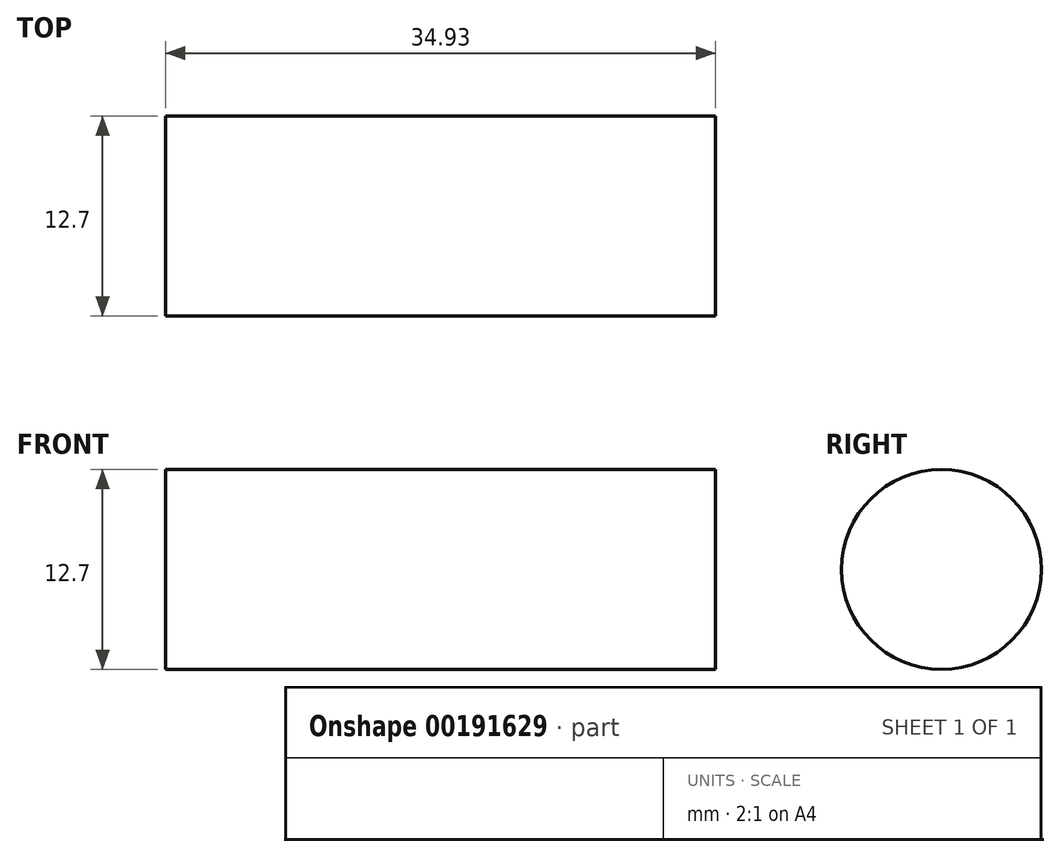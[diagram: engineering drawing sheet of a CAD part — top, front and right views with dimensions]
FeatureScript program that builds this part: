
annotation { "Feature Type Name" : "Feature", "Feature Type Description" : "" }
export const myFeature = defineFeature(function(context is Context, id is Id, definition is map)
    precondition{}
    {
        {
            var Q0;
            Q0=qCreatedBy(makeId("Right.planeOp"),FACE);
            var sketch = newSketch(context, id + "F0", { "sketchPlane" : qUnion([Q0])});
            skCircle(sketch, "E0", {"center": v(0, 0) * mm, "radius": 6.35 * mm});
            skSolve(sketch);
        }
        {
            var Q0;
            Q0=makeQuery(id+"F0.imprint","IMPRINT",FACE,{"disambiguationData":[TD([[makeQuery(id+"F0.imprint","IMPRINT",EDGE,{"derivedFrom":sQuery(id+"F0.wireOp",EDGE,"E0")}),1.0]])]});
            extrude(context, id + "F1", {"entities" : qUnion([Q0]), "depth" : 34.92 * mm});
        }
    });
